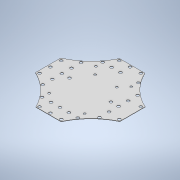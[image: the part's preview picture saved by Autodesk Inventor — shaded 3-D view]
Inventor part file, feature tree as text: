
AUTODESK INVENTOR PART (.ipt)
format: ipt  version: 2020 (Build 240168000, 168)  size: 443,392 bytes
history: native  units: in
note: dims shown in document units (in); Inventor stores cm internally (conversion verified against a paired STEP export)
features: other x2, extrude x1, sketch x1
ambient origin geometry x8: Origin, YZ Plane, XZ Plane, XY Plane, X Axis, Y Axis, Z Axis, Center Point
bodies: Body1 (feature_tree)
feature tree (4):
  other  "pixfalcon_acc_board_light"
  extrude  "Extrusion2"  [1 undecoded]
  sketch  "Sketch1"  dims[d2=0.5in d3=0.0in]
  other  "MeshFeature1"
note: 1 required parameter value undecoded (feature->parameter linkage not recoverable at this tier; creation-order binding heuristic only, values carry confidence <= 0.55)
